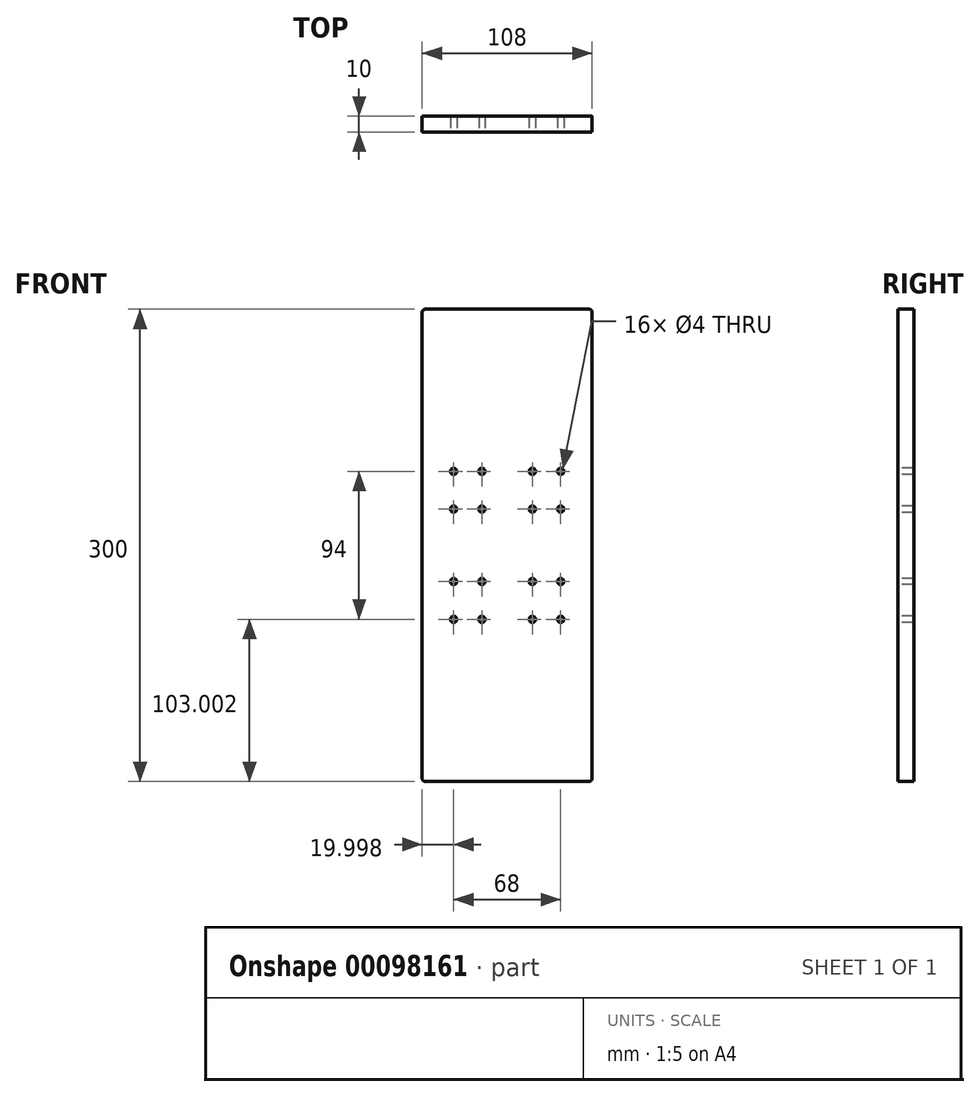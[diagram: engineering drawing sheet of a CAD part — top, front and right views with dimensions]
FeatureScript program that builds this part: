
annotation { "Feature Type Name" : "Feature", "Feature Type Description" : "" }
export const myFeature = defineFeature(function(context is Context, id is Id, definition is map)
    precondition{}
    {
        {
            var Q0;
            Q0=qCreatedBy(makeId("Front.planeOp"),FACE);
            var sketch = newSketch(context, id + "F0", { "sketchPlane" : qUnion([Q0])});
            skLineSegment(sketch, "E0.bottom", {"start": v(-96.52, 309.1) * mm, "end": v(7.48, 309.1) * mm});
            skLineSegment(sketch, "E0.top", {"start": v(-96.52, 9.1) * mm, "end": v(7.48, 9.1) * mm});
            skLineSegment(sketch, "E0.left", {"start": v(-98.52, 307.1) * mm, "end": v(-98.52, 11.1) * mm});
            skLineSegment(sketch, "E0.right", {"start": v(9.48, 307.1) * mm, "end": v(9.48, 11.1) * mm});
            skPoint(sketch, "E1.startSnap0", {"position": v(-44.52, 309.1) * mm});
            skPoint(sketch, "E1.endSnap0", {"position": v(-44.52, 9.1) * mm});
            skPoint(sketch, "E2.visualSharp", {"position": v(-98.52, 309.1) * mm});
            skArc(sketch, "E2.filletArc", {"start": v(-96.52, 309.1) * mm, "mid": v(-97.94, 308.5) * mm, "end": v(-98.52, 307.1) * mm});
            skPoint(sketch, "E3.visualSharp", {"position": v(9.48, 309.1) * mm});
            skArc(sketch, "E3.filletArc", {"start": v(9.48, 307.1) * mm, "mid": v(8.9, 308.5) * mm, "end": v(7.48, 309.1) * mm});
            skPoint(sketch, "E4.visualSharp", {"position": v(-98.52, 9.1) * mm});
            skArc(sketch, "E4.filletArc", {"start": v(-98.52, 11.1) * mm, "mid": v(-97.94, 9.68) * mm, "end": v(-96.52, 9.1) * mm});
            skPoint(sketch, "E5.visualSharp", {"position": v(9.48, 9.1) * mm});
            skArc(sketch, "E5.filletArc", {"start": v(7.48, 9.1) * mm, "mid": v(8.9, 9.68) * mm, "end": v(9.48, 11.1) * mm});
            skSolve(sketch);
        }
        {
            var Q0;
            Q0=makeQuery(id+"F0.imprint","IMPRINT",FACE,{"disambiguationData":[TD([[makeQuery(id+"F0.imprint","IMPRINT",EDGE,{"derivedFrom":sQuery(id+"F0.wireOp",EDGE,"E0.bottom")}),-1.0]])]});
            extrude(context, id + "F1", {"entities" : qUnion([Q0]), "depth" : 10 * mm});
        }
        {
            var Q0;
            Q0=makeQuery(id+"F1.opExtrude","CAP_FACE",FACE,{"disambiguationData":[OSD([sQuery(id+"F0.wireOp",EDGE,"E0.bottom"),sQuery(id+"F0.wireOp",EDGE,"E0.top"),sQuery(id+"F0.wireOp",EDGE,"E0.left"),sQuery(id+"F0.wireOp",EDGE,"E0.right")])],"isStart":false});
            var sketch = newSketch(context, id + "F2", { "sketchPlane" : qUnion([Q0])});
            skPoint(sketch, "E6.endSnap0", {"position": v(-44.52, 9.1) * mm});
            skLineSegment(sketch, "E7", {"start": v(-158.77, 159.1) * mm, "end": v(75.06, 159.1) * mm, "construction": true});
            skPoint(sketch, "E8", {"position": v(-60.52, 206.1) * mm});
            skPoint(sketch, "E9", {"position": v(-78.52, 206.1) * mm});
            skPoint(sketch, "E10", {"position": v(-78.52, 182.1) * mm});
            skLineSegment(sketch, "E11", {"start": v(-44.52, 321.49) * mm, "end": v(-44.52, -12.08) * mm, "construction": true});
            skPoint(sketch, "E12", {"position": v(-60.52, 182.1) * mm});
            skPoint(sketch, "E13.MirrorP", {"position": v(-10.52, 182.1) * mm});
            skPoint(sketch, "E14.MirrorP", {"position": v(-28.52, 182.1) * mm});
            skPoint(sketch, "E15.MirrorP", {"position": v(-28.52, 206.1) * mm});
            skPoint(sketch, "E16.MirrorP", {"position": v(-10.52, 206.1) * mm});
            skPoint(sketch, "E17.MirrorP", {"position": v(-28.52, 136.1) * mm});
            skPoint(sketch, "E18.MirrorP", {"position": v(-10.52, 136.1) * mm});
            skPoint(sketch, "E19.MirrorP", {"position": v(-10.52, 112.1) * mm});
            skPoint(sketch, "E20.MirrorP", {"position": v(-28.52, 112.1) * mm});
            skPoint(sketch, "E21.MirrorP", {"position": v(-78.52, 136.1) * mm});
            skPoint(sketch, "E22.MirrorP", {"position": v(-60.52, 136.1) * mm});
            skPoint(sketch, "E23.MirrorP", {"position": v(-60.52, 112.1) * mm});
            skPoint(sketch, "E24.MirrorP", {"position": v(-78.52, 112.1) * mm});
            skSolve(sketch);
        }
        {
            var Q0;
            Q0=sQuery(id+"F2.wireOp",VERTEX,"E9");
            var Q1;
            Q1=sQuery(id+"F2.wireOp",VERTEX,"E8");
            var Q2;
            Q2=sQuery(id+"F2.wireOp",VERTEX,"E12");
            var Q3;
            Q3=sQuery(id+"F2.wireOp",VERTEX,"E10");
            var Q4;
            Q4=sQuery(id+"F2.wireOp",VERTEX,"E15.MirrorP");
            var Q5;
            Q5=sQuery(id+"F2.wireOp",VERTEX,"E16.MirrorP");
            var Q6;
            Q6=sQuery(id+"F2.wireOp",VERTEX,"E13.MirrorP");
            var Q7;
            Q7=sQuery(id+"F2.wireOp",VERTEX,"E14.MirrorP");
            var Q8;
            Q8=sQuery(id+"F2.wireOp",VERTEX,"E18.MirrorP");
            var Q9;
            Q9=sQuery(id+"F2.wireOp",VERTEX,"E19.MirrorP");
            var Q10;
            Q10=sQuery(id+"F2.wireOp",VERTEX,"E20.MirrorP");
            var Q11;
            Q11=sQuery(id+"F2.wireOp",VERTEX,"E17.MirrorP");
            var Q12;
            Q12=sQuery(id+"F2.wireOp",VERTEX,"E22.MirrorP");
            var Q13;
            Q13=sQuery(id+"F2.wireOp",VERTEX,"E23.MirrorP");
            var Q14;
            Q14=sQuery(id+"F2.wireOp",VERTEX,"E24.MirrorP");
            var Q15;
            Q15=sQuery(id+"F2.wireOp",VERTEX,"E21.MirrorP");
            var Q16;
            Q16=makeQuery(id+"F1.opExtrude","SWEPT_BODY",BODY,{"disambiguationData":[OSD([sQuery(id+"F0.wireOp",EDGE,"E0.bottom"),sQuery(id+"F0.wireOp",EDGE,"E0.top"),sQuery(id+"F0.wireOp",EDGE,"E0.left"),sQuery(id+"F0.wireOp",EDGE,"E0.right"),sQuery(id+"F0.wireOp",EDGE,"E2.filletArc"),sQuery(id+"F0.wireOp",EDGE,"E3.filletArc"),sQuery(id+"F0.wireOp",EDGE,"E4.filletArc"),sQuery(id+"F0.wireOp",EDGE,"E5.filletArc")])]});
            hole(context, id + "F3", {"style" : HoleStyle.SIMPLE, "endStyle" : HoleEndStyle.THROUGH, "holeDiameter" : 4 * mm, "locations" : qUnion([Q0, Q1, Q2, Q3, Q4, Q5, Q6, Q7, Q8, Q9, Q10, Q11, Q12, Q13, Q14, Q15]), "scope" : qUnion([Q16]), "isTappedThrough" : true});
        }
    });
